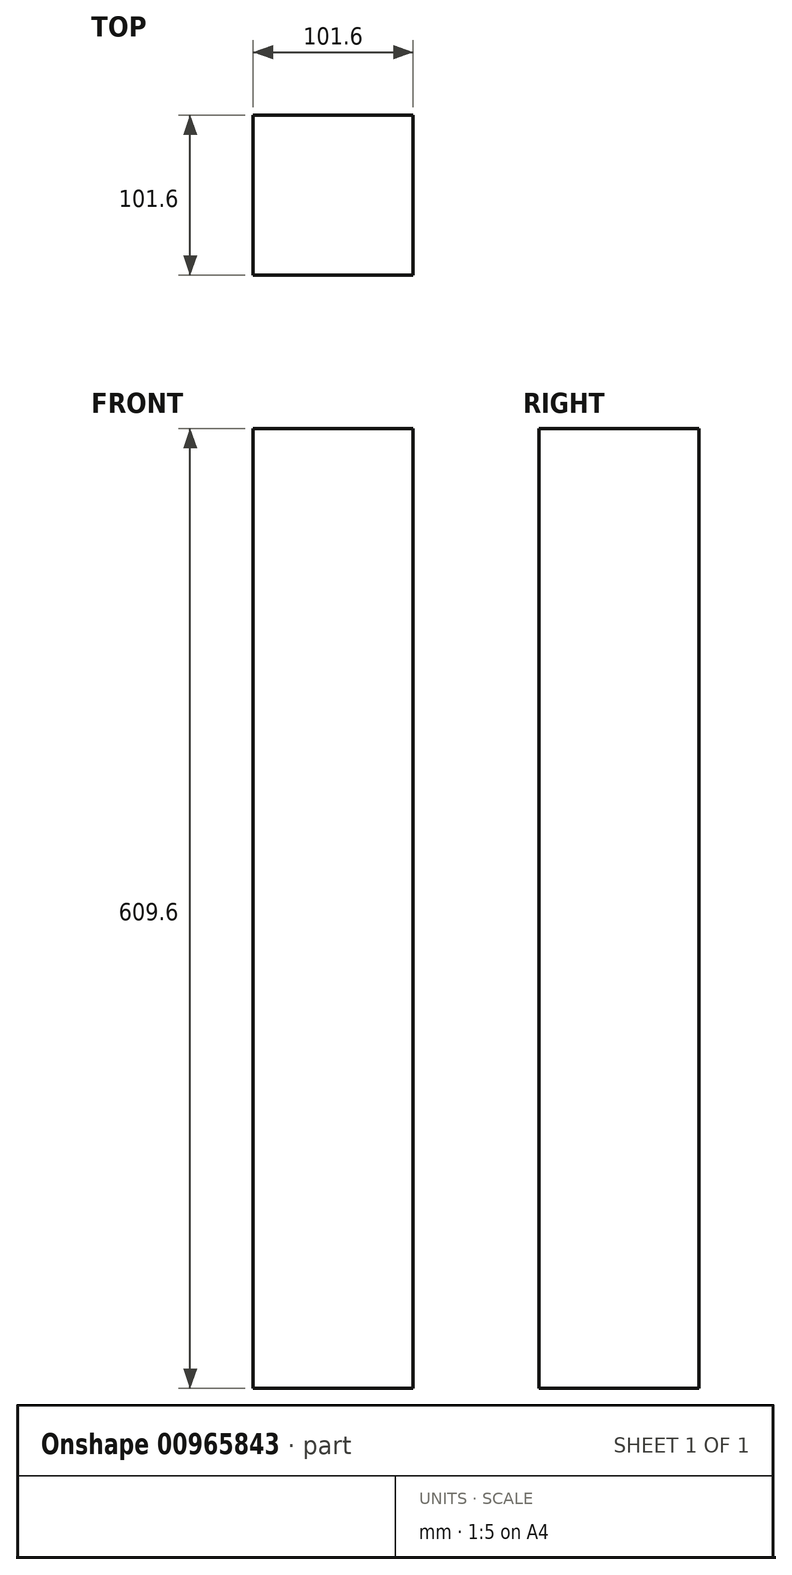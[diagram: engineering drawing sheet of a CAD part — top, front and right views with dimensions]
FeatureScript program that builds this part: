
annotation { "Feature Type Name" : "Feature", "Feature Type Description" : "" }
export const myFeature = defineFeature(function(context is Context, id is Id, definition is map)
    precondition{}
    {
        {
            var Q0;
            Q0=qCreatedBy(makeId("Top.planeOp"),FACE);
            var sketch = newSketch(context, id + "F0", { "sketchPlane" : qUnion([Q0])});
            skLineSegment(sketch, "E0", {"start": v(-82.32, 85.77) * mm, "end": v(19.28, 85.77) * mm});
            skLineSegment(sketch, "E1", {"start": v(19.28, 85.77) * mm, "end": v(19.28, -15.83) * mm});
            skLineSegment(sketch, "E2", {"start": v(19.28, -15.83) * mm, "end": v(-82.32, -15.83) * mm});
            skLineSegment(sketch, "E3", {"start": v(-82.32, -15.83) * mm, "end": v(-82.32, 85.77) * mm});
            skSolve(sketch);
        }
        {
            var Q0;
            Q0=makeQuery(id+"F0.imprint","IMPRINT",FACE,{"disambiguationData":[TD([[makeQuery(id+"F0.imprint","IMPRINT",EDGE,{"derivedFrom":sQuery(id+"F0.wireOp",EDGE,"E0")}),-1.0]])]});
            extrude(context, id + "F1", {"entities" : qUnion([Q0]), "depth" : 609.6 * mm, "offsetDistance" : 25.4 * mm});
        }
    });
